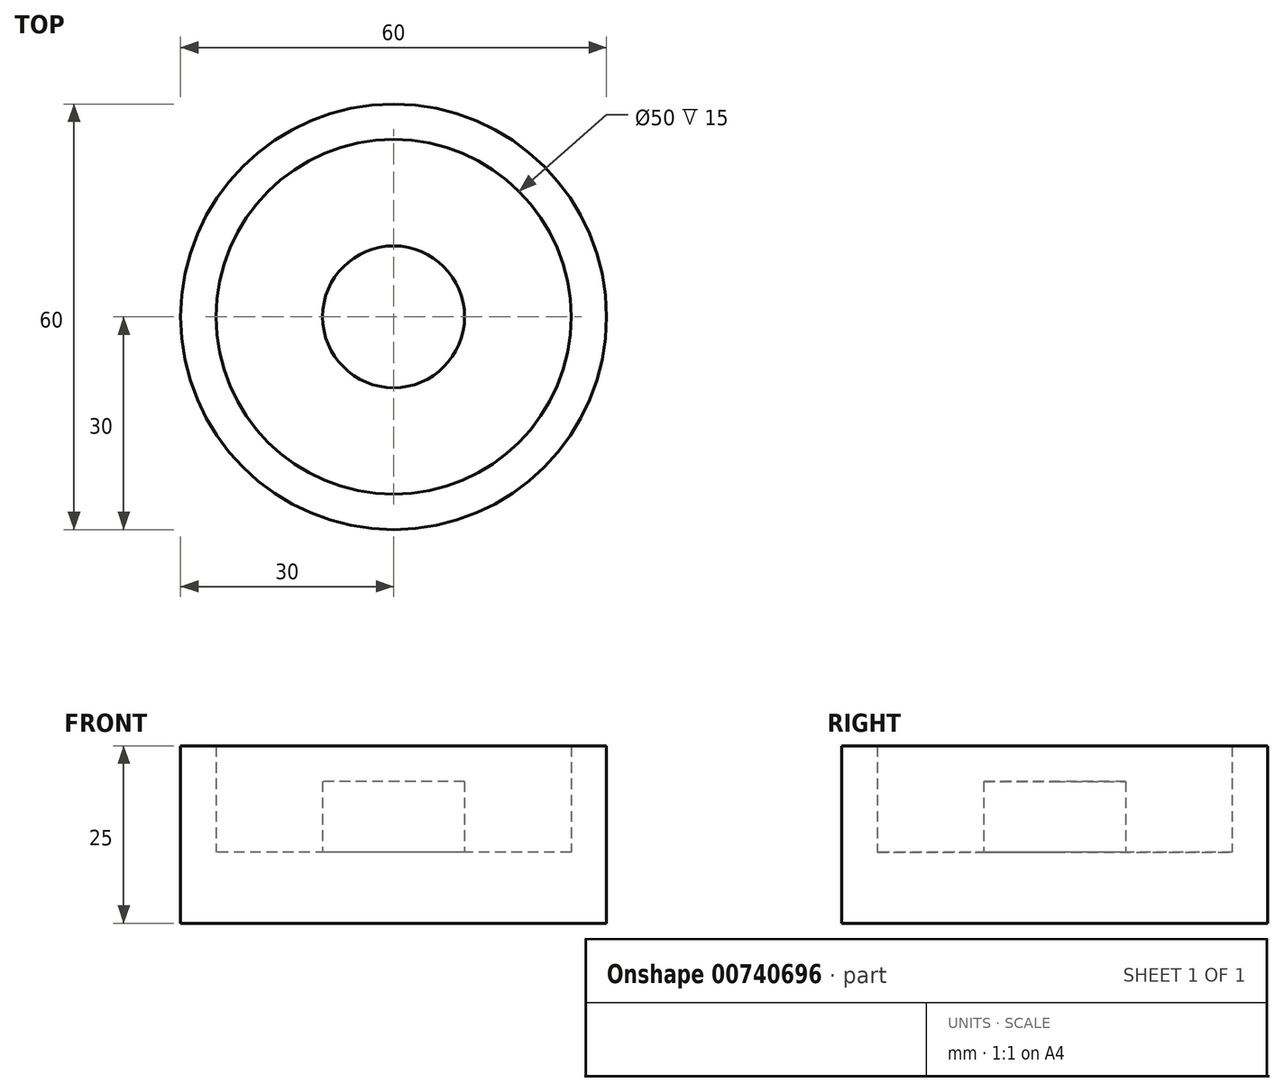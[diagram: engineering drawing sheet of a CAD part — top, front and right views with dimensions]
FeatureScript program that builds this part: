
annotation { "Feature Type Name" : "Feature", "Feature Type Description" : "" }
export const myFeature = defineFeature(function(context is Context, id is Id, definition is map)
    precondition{}
    {
        {
            var Q0;
            Q0=qCreatedBy(makeId("Top.planeOp"),FACE);
            var sketch = newSketch(context, id + "F0", { "sketchPlane" : qUnion([Q0])});
            skCircle(sketch, "E0", {"center": v(0, 0) * mm, "radius": 25 * mm});
            skCircle(sketch, "E1", {"center": v(0, 0) * mm, "radius": 30 * mm});
            skCircle(sketch, "E2", {"center": v(0, 0) * mm, "radius": 10 * mm});
            skSolve(sketch);
        }
        {
            var Q0;
            Q0 = qSketchRegion(id + "F0", true);
            extrude(context, id + "F1", {"entities" : qUnion([Q0]), "depth" : 25 * mm, "offsetDistance" : 25 * mm});
        }
        {
            var Q0;
            Q0=qCreatedBy(makeId("Top.planeOp"),FACE);
            var sketch = newSketch(context, id + "F2", { "sketchPlane" : qUnion([Q0])});
            skCircle(sketch, "E3", {"center": v(0, 0) * mm, "radius": 25 * mm});
            skCircle(sketch, "E4", {"center": v(0, 0) * mm, "radius": 10 * mm});
            skSolve(sketch);
        }
        {
            var Q0;
            Q0 = qSketchRegion(id + "F2", true);
            extrude(context, id + "F3", {"entities" : qUnion([Q0]), "operationType" : NewBodyOperationType.ADD, "depth" : 10 * mm, "offsetDistance" : 25 * mm});
        }
        {
            var Q0;
            Q0=makeQuery(id+"F2.imprint","IMPRINT",FACE,{"disambiguationData":[TD([[makeQuery(id+"F2.imprint","IMPRINT",EDGE,{"derivedFrom":sQuery(id+"F2.wireOp",EDGE,"E4")}),1.0]])]});
            extrude(context, id + "F4", {"entities" : qUnion([Q0]), "operationType" : NewBodyOperationType.ADD, "depth" : 20 * mm, "offsetDistance" : 25 * mm});
        }
    });
